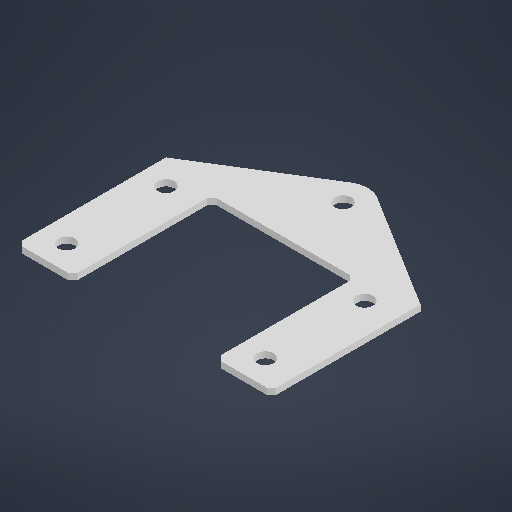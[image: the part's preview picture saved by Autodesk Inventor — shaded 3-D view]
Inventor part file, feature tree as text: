
AUTODESK INVENTOR PART (.ipt)
format: ipt  version: 2025.2 (Build 292293000, 293)  size: 220,672 bytes
history: native  units: in
note: dims shown in document units (in); Inventor stores cm internally (conversion verified against a paired STEP export)
features: extrude x1, sketch x1
ambient origin geometry x8: Origin, YZ Plane, XZ Plane, XY Plane, X Axis, Y Axis, Z Axis, Center Point
bodies: Solid1 (feature_tree)
feature tree (2):
  extrude  "Extrusion1"  Depth=0.0625in TaperAngle=0.0deg
  sketch  "Sketch1"  dims[d0=0.25in d1=0.05in d2=0.05in d3=1.4in d4=0.05in d5=0.05in d6=0.05in d7=0.05in d8=1.4in d9=0.05in d10=0.05in d11=0.05in d12=0.05in d13=0.05in d14=0.05in d16=0.0625in d17=0.0in d18=0.25in d19=0.04in d20=1.45in d21=0.172in]
